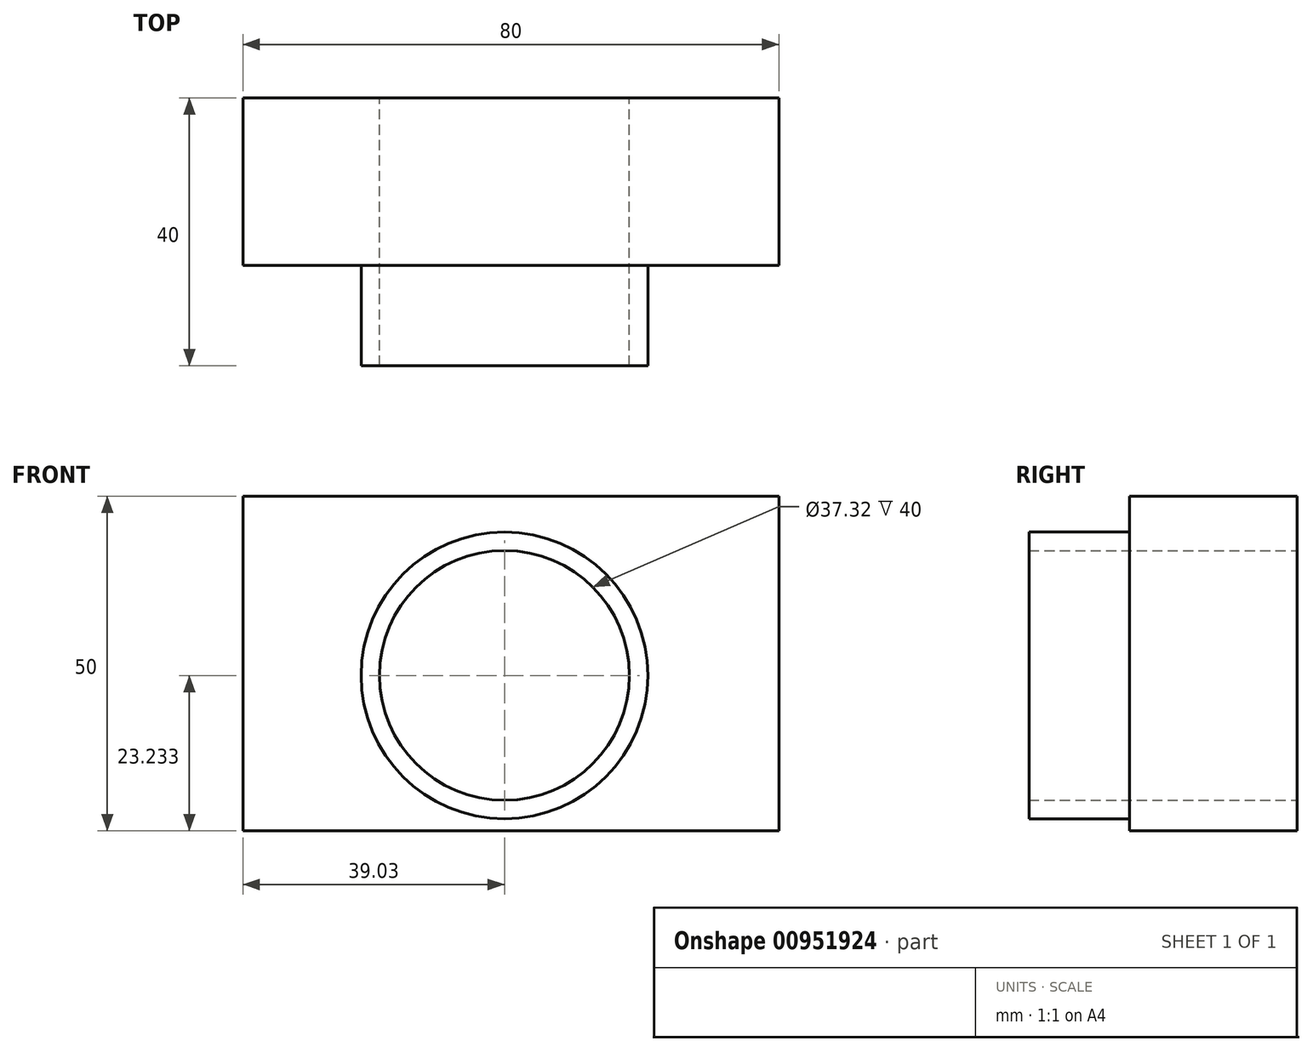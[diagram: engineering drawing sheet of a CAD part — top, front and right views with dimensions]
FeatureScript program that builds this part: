
annotation { "Feature Type Name" : "Feature", "Feature Type Description" : "" }
export const myFeature = defineFeature(function(context is Context, id is Id, definition is map)
    precondition{}
    {
        {
            var Q0;
            Q0=qCreatedBy(makeId("Front.planeOp"),FACE);
            var sketch = newSketch(context, id + "F0", { "sketchPlane" : qUnion([Q0])});
            skLineSegment(sketch, "E0.bottom", {"start": v(-39.03, 12.26) * mm, "end": v(40.97, 12.26) * mm});
            skLineSegment(sketch, "E0.top", {"start": v(-39.03, -37.74) * mm, "end": v(40.97, -37.74) * mm});
            skLineSegment(sketch, "E0.left", {"start": v(-39.03, 12.26) * mm, "end": v(-39.03, -37.74) * mm});
            skLineSegment(sketch, "E0.right", {"start": v(40.97, 12.26) * mm, "end": v(40.97, -37.74) * mm});
            skSolve(sketch);
        }
        {
            var Q0;
            Q0 = qSketchRegion(id + "F0", true);
            extrude(context, id + "F1", {"entities" : qUnion([Q0]), "depth" : 25 * mm, "offsetDistance" : 25 * mm});
        }
        {
            var Q0;
            Q0=qCreatedBy(makeId("Front.planeOp"),FACE);
            var sketch = newSketch(context, id + "F2", { "sketchPlane" : qUnion([Q0])});
            skCircle(sketch, "E1", {"center": v(0, -14.5) * mm, "radius": 18.66 * mm});
            skSolve(sketch);
        }
        {
            var Q0;
            Q0=makeQuery(id+"F2.imprint","IMPRINT",FACE,{"disambiguationData":[TD([[makeQuery(id+"F2.imprint","IMPRINT",EDGE,{"derivedFrom":sQuery(id+"F2.wireOp",EDGE,"E1")}),1.0]])]});
            extrude(context, id + "F3", {"entities" : qUnion([Q0]), "operationType" : NewBodyOperationType.REMOVE, "depth" : 91.2 * mm, "offsetDistance" : 25 * mm, "symmetric" : true});
        }
        {
            var Q0;
            Q0=makeQuery(id+"F1.opExtrude","CAP_FACE",FACE,{"disambiguationData":[OSD([sQuery(id+"F0.wireOp",EDGE,"E0.bottom"),sQuery(id+"F0.wireOp",EDGE,"E0.top"),sQuery(id+"F0.wireOp",EDGE,"E0.left"),sQuery(id+"F0.wireOp",EDGE,"E0.right")])],"isStart":true});
            var sketch = newSketch(context, id + "F4", { "sketchPlane" : qUnion([Q0])});
            skCircle(sketch, "E2", {"center": v(0, -14.5) * mm, "radius": 21.4 * mm});
            skSolve(sketch);
        }
        {
            var Q0;
            Q0=makeQuery(id+"F4.imprint","IMPRINT",FACE,{"disambiguationData":[TD([[makeQuery(id+"F4.imprint","IMPRINT",EDGE,{"derivedFrom":sQuery(id+"F4.wireOp",EDGE,"E2")}),1.0]])]});
            extrude(context, id + "F5", {"entities" : qUnion([Q0]), "operationType" : NewBodyOperationType.ADD, "oppositeDirection" : true, "depth" : 40 * mm, "offsetDistance" : 25 * mm});
        }
    });
